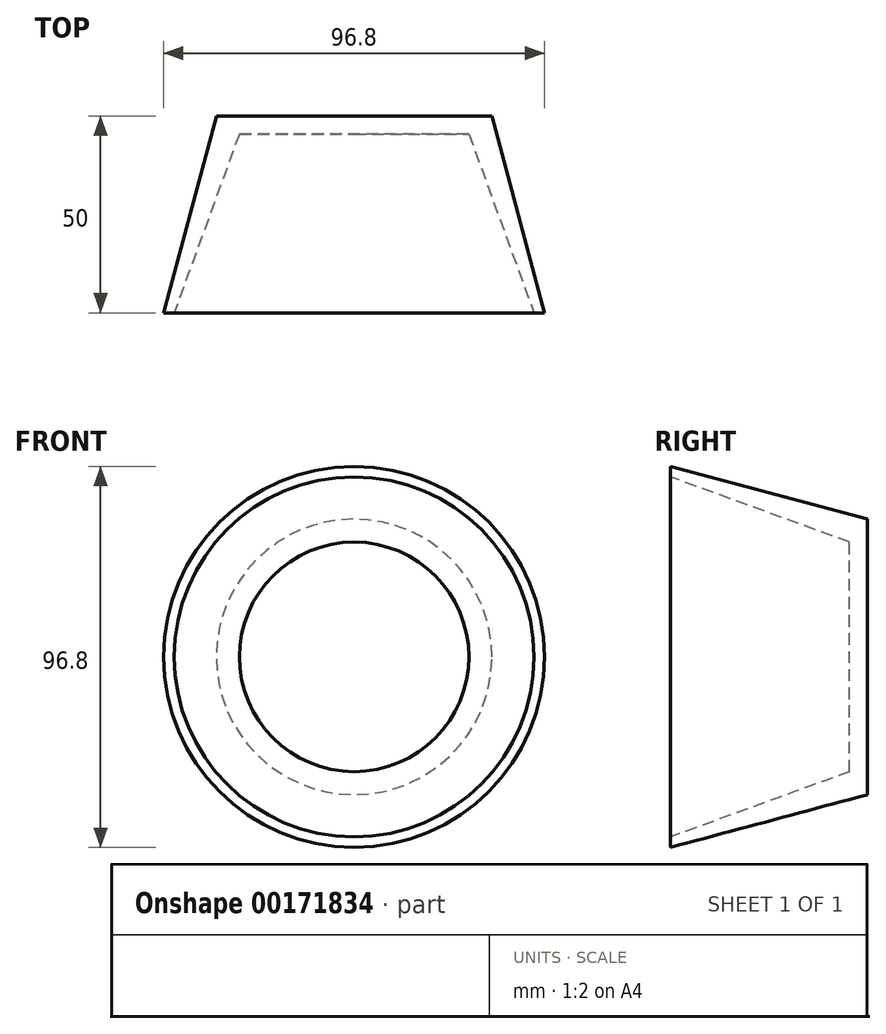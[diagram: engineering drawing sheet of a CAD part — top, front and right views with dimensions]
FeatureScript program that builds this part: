
annotation { "Feature Type Name" : "Feature", "Feature Type Description" : "" }
export const myFeature = defineFeature(function(context is Context, id is Id, definition is map)
    precondition{}
    {
        {
            var Q0;
            Q0=qCreatedBy(makeId("Front.planeOp"),FACE);
            var sketch = newSketch(context, id + "F0", { "sketchPlane" : qUnion([Q0])});
            skCircle(sketch, "E0", {"center": v(0, 0) * mm, "radius": 35 * mm});
            skSolve(sketch);
        }
        {
            var Q0;
            Q0 = qSketchRegion(id + "F0", true);
            extrude(context, id + "F1", {"entities" : qUnion([Q0]), "depth" : 50 * mm, "hasDraft" : true, "draftAngle" : 15 * degree});
        }
        {
            var Q0;
            Q0=makeQuery(id+"F1.opExtrude","CAP_FACE",FACE,{"disambiguationData":[OSD([sQuery(id+"F0.wireOp",EDGE,"E0")])],"isStart":false});
            var sketch = newSketch(context, id + "F2", { "sketchPlane" : qUnion([Q0])});
            skCircle(sketch, "E1", {"center": v(0, 0) * mm, "radius": 45.7 * mm});
            skSolve(sketch);
        }
        {
            var Q0;
            Q0=makeQuery(id+"F2.imprint","IMPRINT",FACE,{"disambiguationData":[TD([[makeQuery(id+"F2.imprint","IMPRINT",EDGE,{"derivedFrom":sQuery(id+"F2.wireOp",EDGE,"E1")}),1.0]])]});
            extrude(context, id + "F3", {"entities" : qUnion([Q0]), "operationType" : NewBodyOperationType.REMOVE, "oppositeDirection" : true, "depth" : 45.47 * mm, "hasDraft" : true, "draftAngle" : 20 * degree, "draftPullDirection" : true});
        }
    });
